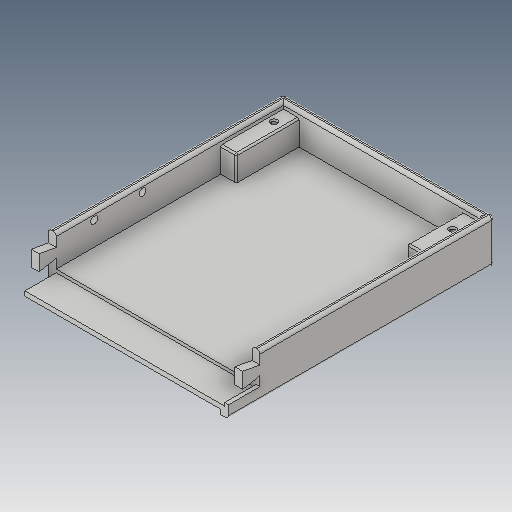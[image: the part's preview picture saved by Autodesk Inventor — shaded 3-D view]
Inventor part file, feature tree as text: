
AUTODESK INVENTOR PART (.ipt)
format: ipt  version: 2019 (Build 230136000, 136)  size: 364,544 bytes
history: native  units: mm
features: extrude x7, sketch x7, other x5, fillet x2, projected_geometry x2, surface_op x1, plane x1
ambient origin geometry x8: Origin, YZ Plane, XZ Plane, XY Plane, X Axis, Y Axis, Z Axis, Center Point
bodies: Solid1 (feature_tree)
feature tree (25):
  extrude  "Extrusion1"  Depth=170.0mm
  extrude  "Extrusion2"  Depth=5.0mm
  extrude  "Extrusion3"  Depth=25.0mm TaperAngle=0.0deg
  fillet  "Fillet1"  Radius=2.0mm
  surface_op  "Sculpt2"
  extrude  "Extrusion4"  TaperAngle=0.0deg  [1 undecoded]
  extrude  "Extrusion5"  Depth=40.0mm
  fillet  "Fillet2"  [1 undecoded]
  extrude  "Extrusion7"  Depth=35.0mm
  plane  "Work Plane1"
  extrude  "Extrusion8"  Depth=16.0mm TaperAngle=0.0deg
  sketch  "Sketch1"  dims[d0=135.0mm d1=170.0mm]
  sketch  "Sketch2"  dims[d2=28.0mm d3=0.0mm d4=5.0mm]
  projected_geometry  "Projected Loop1"
  sketch  "Sketch3"  dims[d5=20.0mm d6=0.0mm d7=25.0mm d8=0.0mm d9=2.0mm]
  projected_geometry  "Projected Loop2"
  sketch  "Sketch4"  dims[d10=0.0mm d11=0.0mm]
  sketch  "Sketch5"  dims[d12=10.0mm d13=40.0mm d14=0.0mm]
  sketch  "Sketch6"  dims[d15=0.0mm d16=35.0mm]
  sketch  "Sketch7"  dims[d17=11.0mm d18=16.0mm d19=0.0mm d20=4.5mm d22=4.0mm d23=4.5mm d24=6.5mm d26=12.0mm d27=0.0mm d28=1.0mm d29=4.5mm d30=4.5mm d31=30.8mm d32=5.0mm d34=90.0mm d37=0.0mm d38=0.0mm d39=-1.5mm d40=7.5mm d41=7.5mm d42=3.15mm d43=0.0mm d44=10.0mm d45=12.5mm]
  other  "Composite2"
  other  "Srf2"
  parser-record x1  (decoder bookkeeping rows leaked as tree rows — omitted from the tree; the rows remain in map.json)
  other  "CaseA.iam"
  other  "Case_A1:1"
note: 2 required parameter values undecoded (feature->parameter linkage not recoverable at this tier; creation-order binding heuristic only, values carry confidence <= 0.55)
note: 1 file-system path scrubbed to <path> (originals preserved in map.json)
